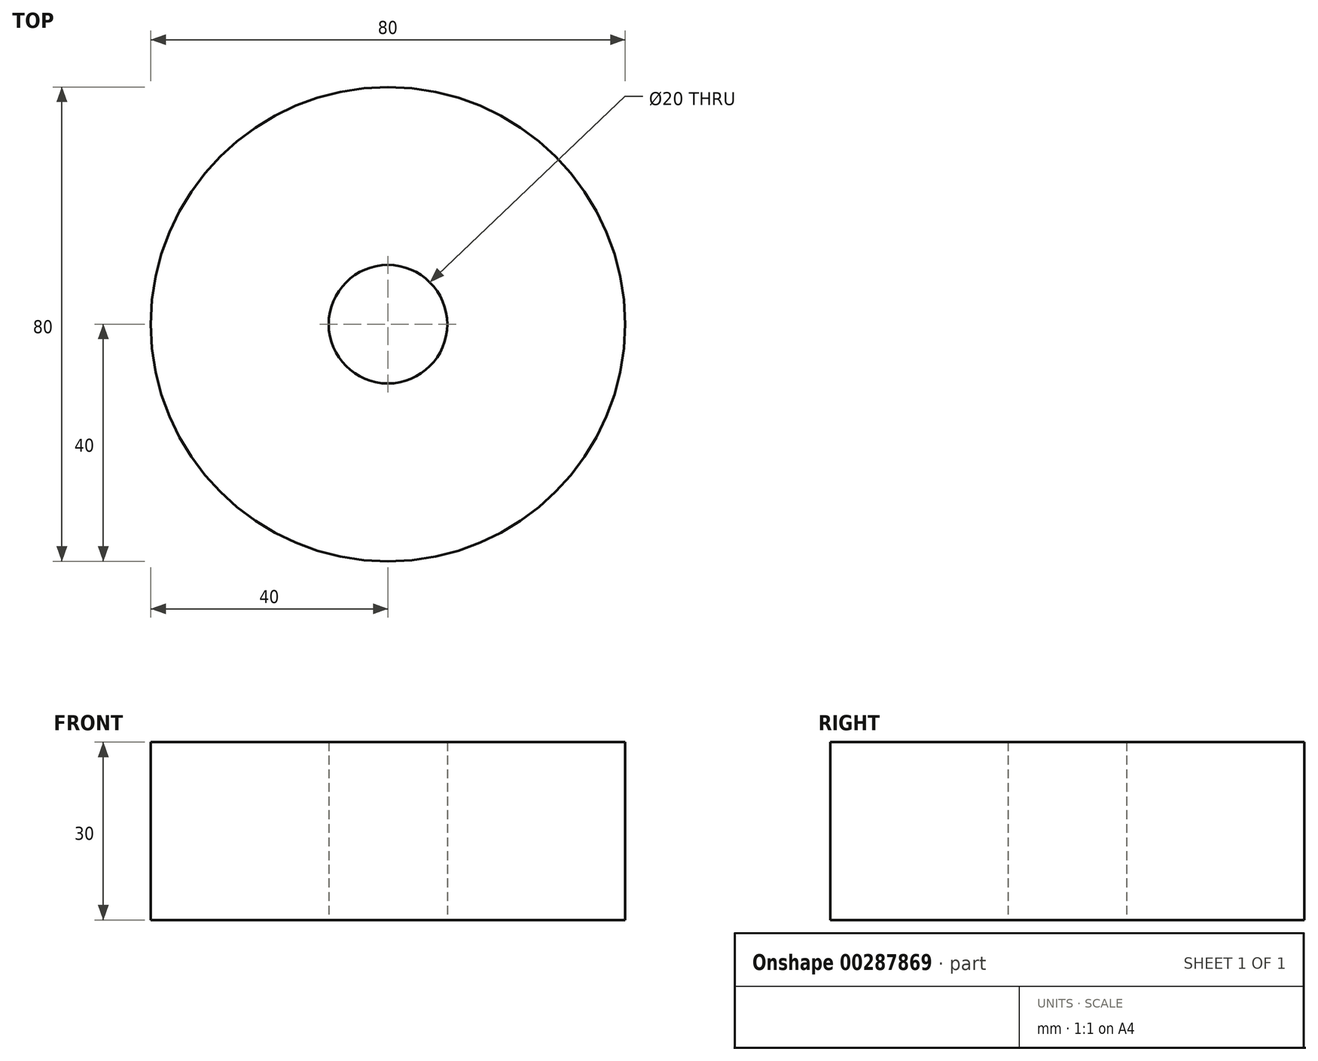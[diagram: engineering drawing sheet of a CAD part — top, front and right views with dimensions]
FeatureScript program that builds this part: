
annotation { "Feature Type Name" : "Feature", "Feature Type Description" : "" }
export const myFeature = defineFeature(function(context is Context, id is Id, definition is map)
    precondition{}
    {
        {
            var Q0;
            Q0=qCreatedBy(makeId("Top.planeOp"),FACE);
            var sketch = newSketch(context, id + "F0", { "sketchPlane" : qUnion([Q0])});
            skCircle(sketch, "E0", {"center": v(0, 0) * mm, "radius": 10 * mm});
            skCircle(sketch, "E1", {"center": v(0, 0) * mm, "radius": 40 * mm});
            skSolve(sketch);
        }
        {
            var Q0;
            Q0 = qSketchRegion(id + "F0", true);
            extrude(context, id + "F1", {"entities" : qUnion([Q0]), "depth" : 30 * mm});
        }
    });
